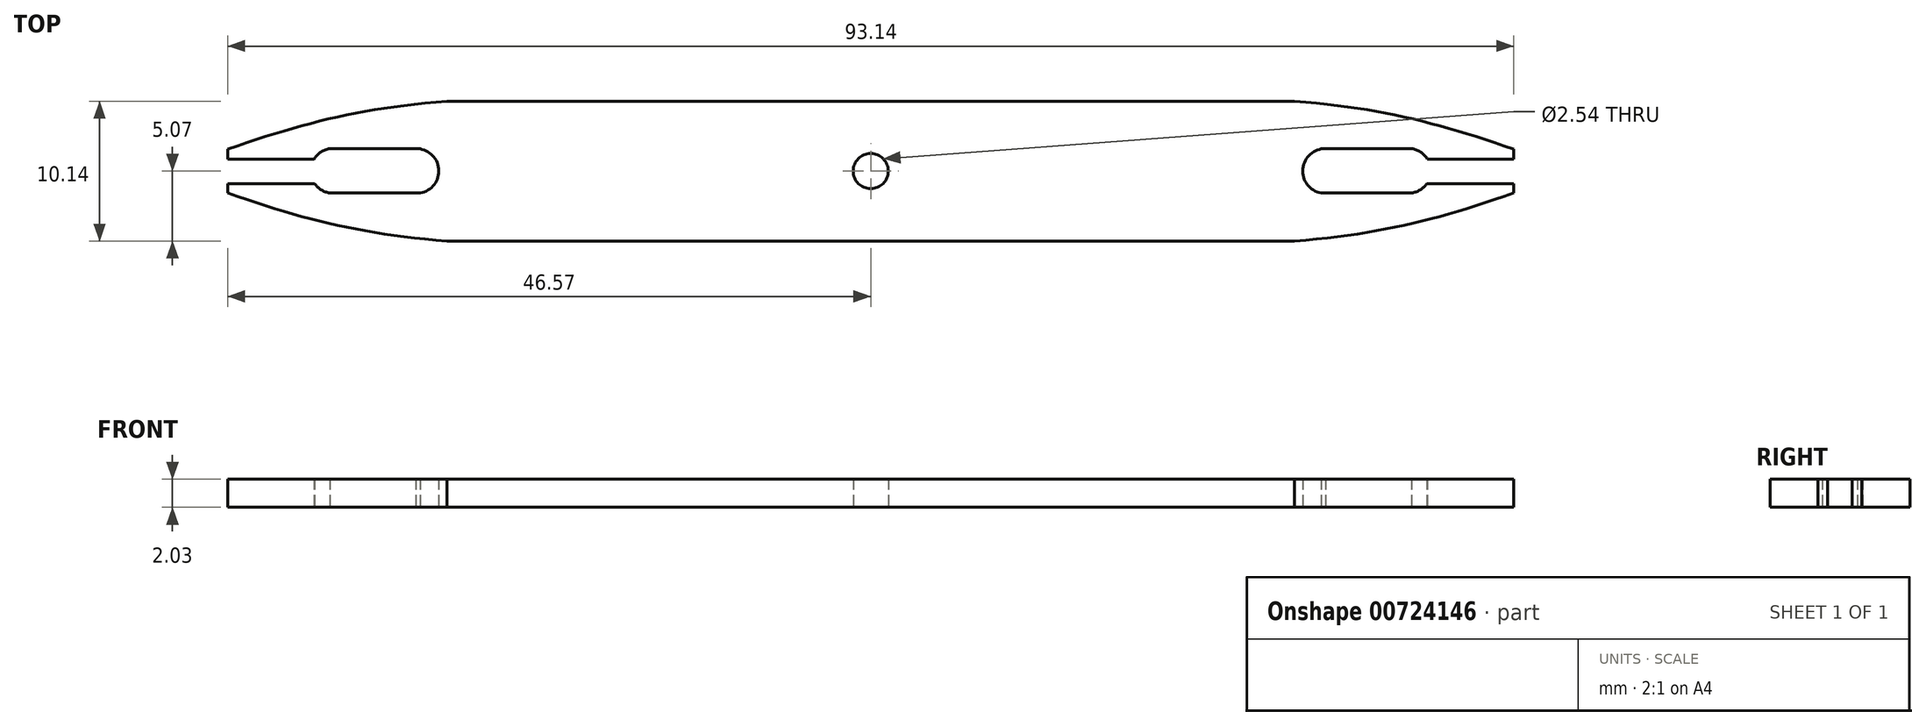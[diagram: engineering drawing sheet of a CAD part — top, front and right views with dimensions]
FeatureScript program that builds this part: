
annotation { "Feature Type Name" : "Feature", "Feature Type Description" : "" }
export const myFeature = defineFeature(function(context is Context, id is Id, definition is map)
    precondition{}
    {
        {
            var Q0;
            Q0=qCreatedBy(makeId("Top.planeOp"),FACE);
            var sketch = newSketch(context, id + "F0", { "sketchPlane" : qUnion([Q0])});
            skLineSegment(sketch, "E0.right", {"start": v(46.57, 1.58) * mm, "end": v(46.57, 0.88) * mm});
            skCircle(sketch, "E1", {"center": v(0, 0) * mm, "radius": 1.27 * mm});
            skPoint(sketch, "E2", {"position": v(46.57, 1.58) * mm});
            skPoint(sketch, "E3", {"position": v(46.57, -0.7) * mm});
            skPoint(sketch, "E4", {"position": v(46.57, -1.7) * mm});
            skPoint(sketch, "E5", {"position": v(46.57, 0.88) * mm});
            skLineSegment(sketch, "E6.bottom", {"start": v(46.57, 0.88) * mm, "end": v(40.3, 0.88) * mm});
            skLineSegment(sketch, "E6.top", {"start": v(46.57, -0.9) * mm, "end": v(40.27, -0.9) * mm});
            skLineSegment(sketch, "E7.trimOffspring", {"start": v(46.57, -0.9) * mm, "end": v(46.57, -1.7) * mm});
            skPoint(sketch, "E8", {"position": v(39.38, 0.88) * mm});
            skArc(sketch, "E9", {"start": v(32.95, 1.63) * mm, "mid": v(31.3, 0.17) * mm, "end": v(32.63, -1.59) * mm});
            skLineSegment(sketch, "E10", {"start": v(32.63, -1.59) * mm, "end": v(39.16, -1.59) * mm});
            skLineSegment(sketch, "E11", {"start": v(32.95, 1.63) * mm, "end": v(39.16, 1.63) * mm});
            skArc(sketch, "E12", {"start": v(39.16, -1.59) * mm, "mid": v(39.79, -1.36) * mm, "end": v(40.27, -0.9) * mm});
            skArc(sketch, "E13.trimOffspring", {"start": v(40.3, 0.88) * mm, "mid": v(39.82, 1.38) * mm, "end": v(39.16, 1.63) * mm});
            skFitSpline(sketch, "E14", {"points": [v(46.57, 1.58) * mm, v(30.69, 5.07) * mm], "startDerivative": vector(-16.35, 5.71) * mm, "endDerivative": vector(-18.94, 1.55) * mm});
            skFitSpline(sketch, "E15.MirrorCS", {"points": [v(46.57, -1.58) * mm, v(30.69, -5.07) * mm], "startDerivative": vector(-16.35, -5.71) * mm, "endDerivative": vector(-18.94, -1.55) * mm});
            skPoint(sketch, "E16.orphan", {"position": v(46.57, 5.07) * mm});
            skPoint(sketch, "E0.top.end.orphan", {"position": v(46.57, -5.09) * mm});
            skLineSegment(sketch, "E17.MirrorCS", {"start": v(-46.57, -0.9) * mm, "end": v(-46.57, -1.7) * mm});
            skLineSegment(sketch, "E18.MirrorCS", {"start": v(-46.57, 1.58) * mm, "end": v(-46.57, 0.88) * mm});
            skArc(sketch, "E19.MirrorCS", {"start": v(-40.3, 0.88) * mm, "mid": v(-39.82, 1.38) * mm, "end": v(-39.16, 1.63) * mm});
            skArc(sketch, "E20.MirrorCS", {"start": v(-39.16, -1.59) * mm, "mid": v(-39.79, -1.36) * mm, "end": v(-40.27, -0.9) * mm});
            skPoint(sketch, "E21.MirrorP", {"position": v(-46.57, -0.7) * mm});
            skLineSegment(sketch, "E22.MirrorCS", {"start": v(-32.95, 1.63) * mm, "end": v(-39.16, 1.63) * mm});
            skLineSegment(sketch, "E23.MirrorCS", {"start": v(-32.63, -1.59) * mm, "end": v(-39.16, -1.59) * mm});
            skArc(sketch, "E24.MirrorCS", {"start": v(-32.95, 1.63) * mm, "mid": v(-31.3, 0.17) * mm, "end": v(-32.63, -1.59) * mm});
            skLineSegment(sketch, "E25.MirrorCS", {"start": v(-46.57, -0.9) * mm, "end": v(-40.27, -0.9) * mm});
            skLineSegment(sketch, "E26.MirrorCS", {"start": v(-46.57, 0.88) * mm, "end": v(-40.3, 0.88) * mm});
            skPoint(sketch, "E27.MirrorP", {"position": v(-39.38, 0.88) * mm});
            skPoint(sketch, "E28.MirrorP", {"position": v(-46.57, 0.88) * mm});
            skPoint(sketch, "E29.MirrorP", {"position": v(-46.57, -1.7) * mm});
            skFitSpline(sketch, "E30.MirrorCS", {"points": [v(-46.57, 1.58) * mm, v(-30.69, 5.07) * mm], "startDerivative": vector(16.35, 5.71) * mm, "endDerivative": vector(18.94, 1.55) * mm});
            skFitSpline(sketch, "E31.MirrorCS", {"points": [v(-46.57, -1.58) * mm, v(-30.69, -5.07) * mm], "startDerivative": vector(16.35, -5.71) * mm, "endDerivative": vector(18.94, -1.55) * mm});
            skLineSegment(sketch, "E32.trimOffspring", {"start": v(-30.69, 5.07) * mm, "end": v(30.69, 5.07) * mm});
            skLineSegment(sketch, "E33", {"start": v(-30.69, -5.07) * mm, "end": v(30.69, -5.07) * mm});
            skSolve(sketch);
        }
        {
            var Q0;
            Q0=makeQuery(id+"F0.imprint","IMPRINT",FACE,{"disambiguationData":[TD([[makeQuery(id+"F0.imprint","IMPRINT",EDGE,{"derivedFrom":sQuery(id+"F0.wireOp",EDGE,"E0.right")}),-1.0]])]});
            extrude(context, id + "F1", {"entities" : qUnion([Q0]), "depth" : 2.03 * mm, "offsetDistance" : 25.4 * mm});
        }
    });
